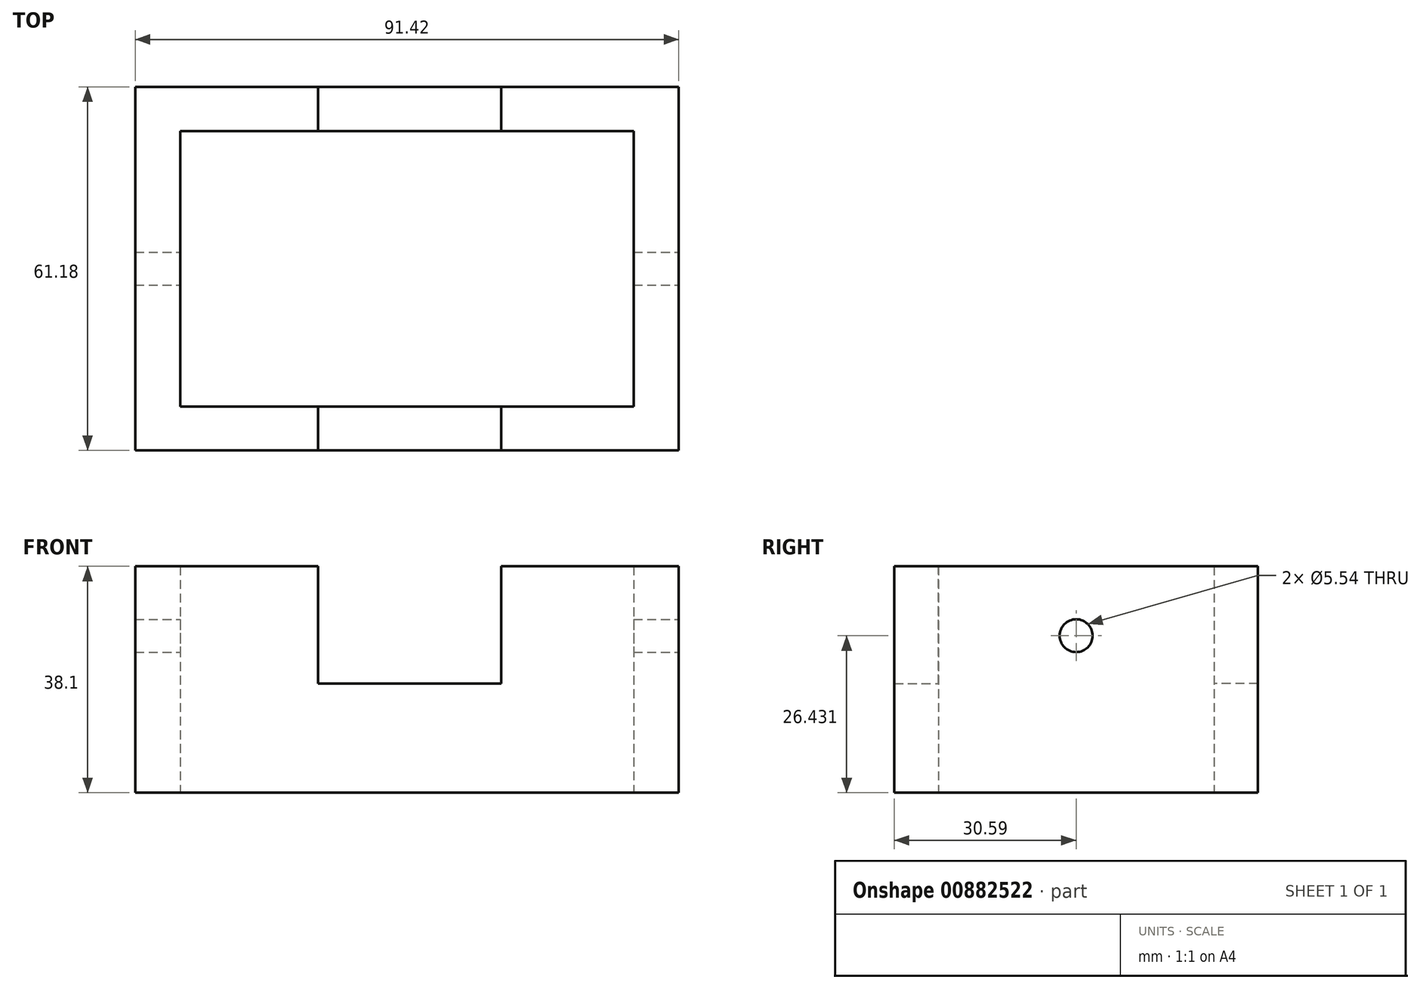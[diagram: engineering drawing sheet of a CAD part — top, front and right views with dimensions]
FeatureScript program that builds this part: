
annotation { "Feature Type Name" : "Feature", "Feature Type Description" : "" }
export const myFeature = defineFeature(function(context is Context, id is Id, definition is map)
    precondition{}
    {
        {
            var Q0;
            Q0=qCreatedBy(makeId("Top.planeOp"),FACE);
            var sketch = newSketch(context, id + "F0", { "sketchPlane" : qUnion([Q0])});
            skLineSegment(sketch, "E0.bottom", {"start": v(45.71, -30.59) * mm, "end": v(-45.71, -30.59) * mm});
            skLineSegment(sketch, "E0.top", {"start": v(45.71, 30.59) * mm, "end": v(-45.71, 30.59) * mm});
            skLineSegment(sketch, "E0.left", {"start": v(45.71, -30.59) * mm, "end": v(45.71, 30.59) * mm});
            skLineSegment(sketch, "E0.right", {"start": v(-45.71, -30.59) * mm, "end": v(-45.71, 30.59) * mm});
            skPoint(sketch, "E0.middle", {"position": v(0, 0) * mm});
            skLineSegment(sketch, "E1.bottom", {"start": v(38.1, -23.17) * mm, "end": v(-38.1, -23.17) * mm});
            skLineSegment(sketch, "E1.top", {"start": v(38.1, 23.17) * mm, "end": v(-38.1, 23.17) * mm});
            skLineSegment(sketch, "E1.left", {"start": v(38.1, -23.17) * mm, "end": v(38.1, 23.17) * mm});
            skLineSegment(sketch, "E1.right", {"start": v(-38.1, -23.17) * mm, "end": v(-38.1, 23.17) * mm});
            skSolve(sketch);
        }
        {
            var Q0;
            Q0=makeQuery(id+"F0.imprint","IMPRINT",FACE,{"disambiguationData":[TD([[makeQuery(id+"F0.imprint","IMPRINT",EDGE,{"derivedFrom":sQuery(id+"F0.wireOp",EDGE,"E0.bottom")}),-1.0]])]});
            extrude(context, id + "F1", {"entities" : qUnion([Q0]), "depth" : 38.1 * mm, "offsetDistance" : 25.4 * mm});
        }
        {
            var Q0;
            Q0=qCreatedBy(makeId("Front.planeOp"),FACE);
            var sketch = newSketch(context, id + "F2", { "sketchPlane" : qUnion([Q0])});
            skLineSegment(sketch, "E2.bottom", {"start": v(-14.98, 38.5) * mm, "end": v(15.86, 38.5) * mm});
            skLineSegment(sketch, "E2.top", {"start": v(-14.98, 18.4) * mm, "end": v(15.86, 18.4) * mm});
            skLineSegment(sketch, "E2.left", {"start": v(-14.98, 38.5) * mm, "end": v(-14.98, 18.4) * mm});
            skLineSegment(sketch, "E2.right", {"start": v(15.86, 38.5) * mm, "end": v(15.86, 18.4) * mm});
            skSolve(sketch);
        }
        {
            var Q0;
            Q0=qSketchRegion(id+"F2",true);
            extrude(context, id + "F3", {"entities" : qUnion([Q0]), "operationType" : NewBodyOperationType.REMOVE, "depth" : 62.74 * mm, "offsetDistance" : 25.4 * mm});
        }
        {
            var Q0;
            Q0=qSketchRegion(id+"F2",true);
            extrude(context, id + "F4", {"entities" : qUnion([Q0]), "operationType" : NewBodyOperationType.REMOVE, "oppositeDirection" : true, "depth" : 41.9 * mm, "offsetDistance" : 25.4 * mm});
        }
        {
            var Q0;
            Q0=makeQuery(id+"F1.opExtrude","SWEPT_FACE",FACE,{"disambiguationData":[OSD([sQuery(id+"F0.wireOp",EDGE,"E0.left")])]});
            var sketch = newSketch(context, id + "F5", { "sketchPlane" : qUnion([Q0])});
            skCircle(sketch, "E3", {"center": v(0, 26.43) * mm, "radius": 2.77 * mm});
            skSolve(sketch);
        }
        {
            var Q0;
            Q0=qSketchRegion(id+"F5",true);
            var Q1;
            Q1=sQuery(id+"F5.wireOp",EDGE,"E3");
            extrude(context, id + "F6", {"entities" : qUnion([Q0]), "operationType" : NewBodyOperationType.REMOVE, "surfaceEntities" : qUnion([Q1]), "oppositeDirection" : true, "depth" : 103.63 * mm, "offsetDistance" : 25.4 * mm});
        }
    });
